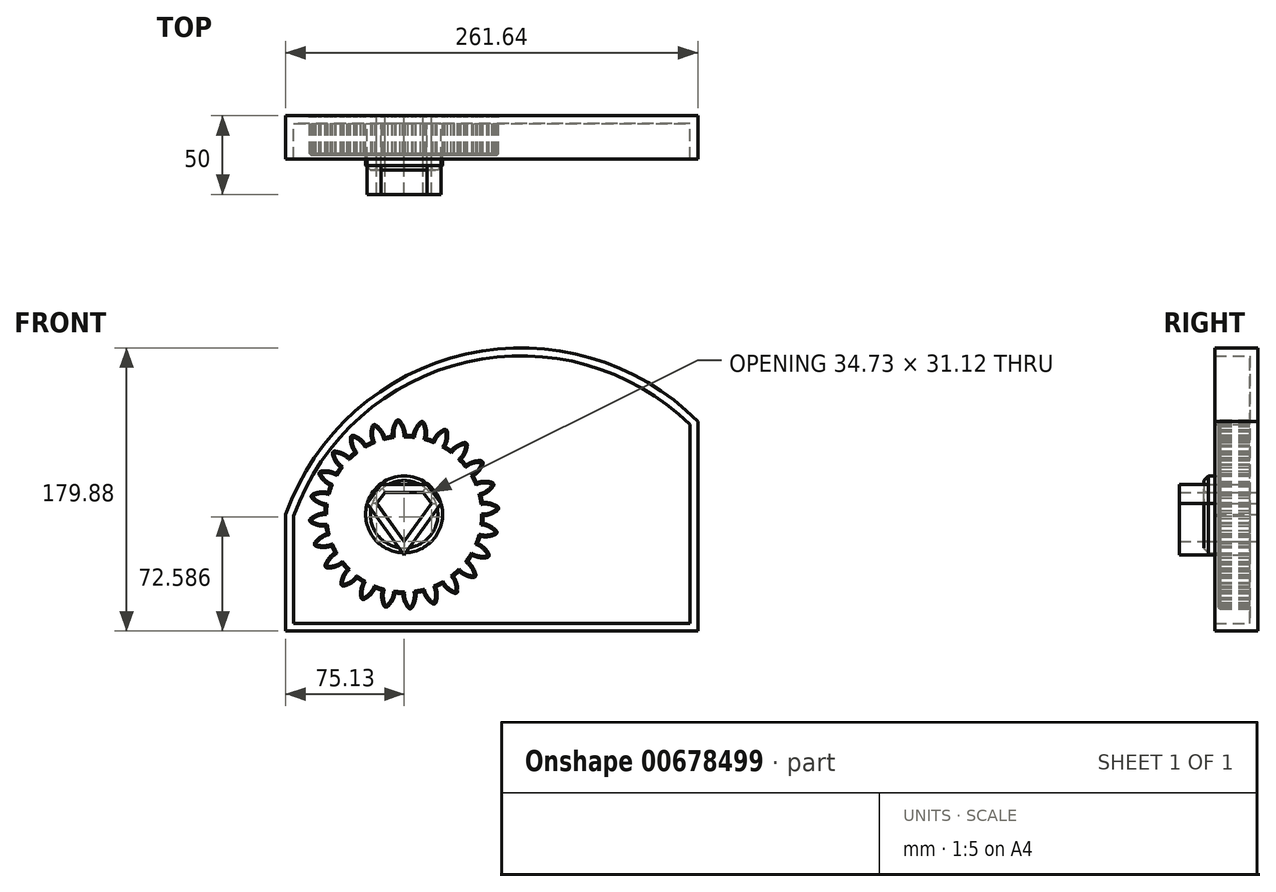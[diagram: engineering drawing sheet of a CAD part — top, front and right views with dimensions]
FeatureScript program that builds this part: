
annotation { "Feature Type Name" : "Feature", "Feature Type Description" : "" }
export const myFeature = defineFeature(function(context is Context, id is Id, definition is map)
    precondition{}
    {
        {
            var Q0;
            Q0=qCreatedBy(makeId("Front.planeOp"),FACE);
            var sketch = newSketch(context, id + "F0", { "sketchPlane" : qUnion([Q0])});
            skCircle(sketch, "E0", {"center": v(0, 0) * mm, "radius": 50.27 * mm});
            skCircle(sketch, "E1", {"center": v(0, 0) * mm, "radius": 54.9 * mm, "construction": true});
            skCircle(sketch, "E2", {"center": v(0, 0) * mm, "radius": 59.42 * mm, "construction": true});
            skLineSegment(sketch, "E3", {"start": v(0, 0) * mm, "end": v(0, 73.6) * mm, "construction": true});
            skLineSegment(sketch, "E4", {"start": v(0, 0) * mm, "end": v(-4.82, 73.6) * mm, "construction": true});
            skLineSegment(sketch, "E5", {"start": v(0, 54.9) * mm, "end": v(-59.15, 54.9) * mm, "construction": true});
            skLineSegment(sketch, "E6", {"start": v(0, 54.9) * mm, "end": v(-59.15, 33.38) * mm, "construction": true});
            skCircle(sketch, "E7", {"center": v(0, 0) * mm, "radius": 51.6 * mm, "construction": true});
            skCircle(sketch, "E8", {"center": v(0, 54.9) * mm, "radius": 14.6 * mm, "construction": true});
            skCircle(sketch, "E9", {"center": v(-13.72, 49.91) * mm, "radius": 14.6 * mm, "construction": true});
            skArc(sketch, "E10", {"start": v(0, 54.9) * mm, "mid": v(-1.1, 57.25) * mm, "end": v(-2.6, 59.37) * mm});
            skArc(sketch, "E11", {"start": v(0.88, 50.27) * mm, "mid": v(0.63, 52.62) * mm, "end": v(0, 54.9) * mm});
            skArc(sketch, "E12.MirrorCS", {"start": v(-7.17, 54.44) * mm, "mid": v(-6.38, 56.9) * mm, "end": v(-5.18, 59.2) * mm});
            skArc(sketch, "E13.MirrorCS", {"start": v(-7.43, 49.72) * mm, "mid": v(-7.5, 52.1) * mm, "end": v(-7.17, 54.44) * mm});
            skArc(sketch, "E14", {"start": v(-2.6, 59.37) * mm, "mid": v(-3.93, 59.96) * mm, "end": v(-5.18, 59.2) * mm});
            skCircle(sketch, "E15", {"center": v(0, 0) * mm, "radius": 24.42 * mm});
            skLineSegment(sketch, "E16", {"start": v(-0.11, 14.02) * mm, "end": v(-12.06, 14.02) * mm});
            skLineSegment(sketch, "E17", {"start": v(-17.36, 7.04) * mm, "end": v(-12.06, 14.02) * mm});
            skLineSegment(sketch, "E18.MirrorCS", {"start": v(17.36, 7.04) * mm, "end": v(12.06, 14.02) * mm});
            skLineSegment(sketch, "E19.MirrorCS", {"start": v(0.11, 14.02) * mm, "end": v(12.06, 14.02) * mm});
            skLineSegment(sketch, "E20", {"start": v(-0.11, -14.36) * mm, "end": v(0, -14.5) * mm});
            skLineSegment(sketch, "E21", {"start": v(0, -14.5) * mm, "end": v(0.11, -14.36) * mm});
            skLineSegment(sketch, "E22", {"start": v(-17.36, 7.04) * mm, "end": v(0, -17.1) * mm});
            skLineSegment(sketch, "E23.MirrorCS", {"start": v(17.36, 7.04) * mm, "end": v(0, -17.1) * mm});
            skLineSegment(sketch, "E24", {"start": v(-0.11, 14.02) * mm, "end": v(0.11, 14.02) * mm});
            skSolve(sketch);
        }
        {
            var Q0;
            {var subQ0=sQuery(id+"F0.wireOp",EDGE,"E0");var subQ1=makeQuery(id+"F0.imprint","INTERSECT",VERTEX,{"derivedFrom":[subQ0,sQuery(id+"F0.wireOp",EDGE,"E11")]});Q0=makeQuery(id+"F0.imprint","IMPRINT",FACE,{"disambiguationData":[TD([[makeQuery(id+"F0.imprint","IMPRINT",EDGE,{"disambiguationData":[TD([[subQ1,-1.0]])],"derivedFrom":subQ0}),1.0]])]});}
            var Q1;
            Q1=makeQuery(id+"F0.imprint","IMPRINT",FACE,{"disambiguationData":[TD([[makeQuery(id+"F0.imprint","IMPRINT",EDGE,{"derivedFrom":sQuery(id+"F0.wireOp",EDGE,"E10")}),1.0]])]});
            extrude(context, id + "F1", {"entities" : qUnion([Q0, Q1]), "depth" : 25 * mm, "offsetDistance" : 25 * mm});
        }
        {
            var Q0;
            Q0=makeQuery(id+"F1.opExtrude","CAP_EDGE",EDGE,{"disambiguationData":[OSD([sQuery(id+"F0.wireOp",EDGE,"E0")])],"isStart":false});
            var Q1;
            Q1=makeQuery(id+"F1.opExtrude","CAP_EDGE",EDGE,{"disambiguationData":[OSD([sQuery(id+"F0.wireOp",EDGE,"E11")])],"isStart":false});
            var Q2;
            Q2=makeQuery(id+"F1.opExtrude","CAP_EDGE",EDGE,{"disambiguationData":[OSD([sQuery(id+"F0.wireOp",EDGE,"E13.MirrorCS")])],"isStart":false});
            var Q3;
            Q3=makeQuery(id+"F1.opExtrude","CAP_EDGE",EDGE,{"disambiguationData":[OSD([sQuery(id+"F0.wireOp",EDGE,"E10")])],"isStart":false});
            var Q4;
            Q4=makeQuery(id+"F1.opExtrude","CAP_EDGE",EDGE,{"disambiguationData":[OSD([sQuery(id+"F0.wireOp",EDGE,"E12.MirrorCS")])],"isStart":false});
            var Q5;
            Q5=makeQuery(id+"F1.opExtrude","CAP_EDGE",EDGE,{"disambiguationData":[OSD([sQuery(id+"F0.wireOp",EDGE,"E14")])],"isStart":false});
            chamfer(context, id + "F2", {"entities" : qUnion([Q0, Q1, Q2, Q3, Q4, Q5]), "width" : 1 * mm, "tangentPropagation" : true});
        }
        {
            var Q0;
            Q0=makeQuery(id+"F1.opExtrude","SWEPT_BODY",BODY,{"disambiguationData":[OSD([sQuery(id+"F0.wireOp",EDGE,"E0"),sQuery(id+"F0.wireOp",EDGE,"E10"),sQuery(id+"F0.wireOp",EDGE,"E11"),sQuery(id+"F0.wireOp",EDGE,"E12.MirrorCS"),sQuery(id+"F0.wireOp",EDGE,"E13.MirrorCS"),sQuery(id+"F0.wireOp",EDGE,"E14"),sQuery(id+"F0.wireOp",EDGE,"E15")])]});
            var Q1;
            Q1=makeQuery(id+"F1.opExtrude","SWEPT_FACE",FACE,{"disambiguationData":[OSD([sQuery(id+"F0.wireOp",EDGE,"E0")])]});
            circularPattern(context, id + "F3", {"entities" : qUnion([Q0]), "axis" : qUnion([Q1]), "angle" : 360 * degree, "instanceCount" : 24, "equalSpace" : true});
        }
        {
            var Q0;
            Q0=makeQuery(id+"F0.imprint","IMPRINT",FACE,{"disambiguationData":[TD([[makeQuery(id+"F0.imprint","IMPRINT",EDGE,{"derivedFrom":sQuery(id+"F0.wireOp",EDGE,"E15")}),1.0]])]});
            extrude(context, id + "F4", {"entities" : qUnion([Q0]), "operationType" : NewBodyOperationType.ADD, "depth" : 34.5 * mm, "offsetDistance" : 25 * mm});
        }
        {
            var Q0;
            Q0=makeQuery(id+"F4.opExtrude","CAP_EDGE",EDGE,{"disambiguationData":[OSD([sQuery(id+"F0.wireOp",EDGE,"E15")])],"isStart":false});
            chamfer(context, id + "F5", {"entities" : qUnion([Q0]), "width" : 3 * mm, "tangentPropagation" : true});
        }
        {
            var Q0;
            Q0=makeQuery(id+"F4.opExtrude","CAP_EDGE",EDGE,{"disambiguationData":[OSD([sQuery(id+"F0.wireOp",EDGE,"E17")])],"isStart":false});
            var Q1;
            Q1=makeQuery(id+"F4.opExtrude","CAP_EDGE",EDGE,{"disambiguationData":[OSD([sQuery(id+"F0.wireOp",EDGE,"E16"),sQuery(id+"F0.wireOp",EDGE,"E19.MirrorCS"),sQuery(id+"F0.wireOp",EDGE,"E24")])],"isStart":false});
            var Q2;
            Q2=makeQuery(id+"F4.opExtrude","CAP_EDGE",EDGE,{"disambiguationData":[OSD([sQuery(id+"F0.wireOp",EDGE,"E18.MirrorCS")])],"isStart":false});
            var Q3;
            Q3=makeQuery(id+"F4.opExtrude","CAP_EDGE",EDGE,{"disambiguationData":[OSD([sQuery(id+"F0.wireOp",EDGE,"E23.MirrorCS")])],"isStart":false});
            var Q4;
            Q4=makeQuery(id+"F4.opExtrude","CAP_EDGE",EDGE,{"disambiguationData":[OSD([sQuery(id+"F0.wireOp",EDGE,"E22")])],"isStart":false});
            fillet(context, id + "F6", {"entities" : qUnion([Q0, Q1, Q2, Q3, Q4]), "radius" : 2 * mm, "tangentPropagation" : true, "allowEdgeOverflow" : false});
        }
        {
            var Q0;
            Q0=qCreatedBy(makeId("Front.planeOp"),FACE);
            var sketch = newSketch(context, id + "F7", { "sketchPlane" : qUnion([Q0])});
            skLineSegment(sketch, "E25", {"start": v(-75.13, 0) * mm, "end": v(-75.13, -74.2) * mm});
            skLineSegment(sketch, "E26", {"start": v(-75.13, -74.2) * mm, "end": v(186.5, -74.2) * mm});
            skLineSegment(sketch, "E27", {"start": v(186.5, -74.2) * mm, "end": v(186.5, 59.11) * mm});
            skArc(sketch, "E28", {"start": v(186.5, 59.11) * mm, "mid": v(39.37, 101.8) * mm, "end": v(-75.13, 0) * mm});
            skLineSegment(sketch, "E29", {"start": v(-0.11, 13.95) * mm, "end": v(-12.06, 13.95) * mm});
            skLineSegment(sketch, "E30", {"start": v(-17.36, 6.98) * mm, "end": v(-12.06, 13.95) * mm});
            skLineSegment(sketch, "E31.MirrorCS", {"start": v(17.36, 6.98) * mm, "end": v(12.06, 13.95) * mm});
            skLineSegment(sketch, "E32.MirrorCS", {"start": v(0.11, 13.95) * mm, "end": v(12.06, 13.95) * mm});
            skLineSegment(sketch, "E33", {"start": v(-17.36, 6.98) * mm, "end": v(0, -17.16) * mm});
            skLineSegment(sketch, "E34.MirrorCS", {"start": v(17.36, 6.98) * mm, "end": v(0, -17.16) * mm});
            skLineSegment(sketch, "E35", {"start": v(-0.11, 13.95) * mm, "end": v(0.11, 13.95) * mm});
            skSolve(sketch);
        }
        {
            var Q0;
            Q0 = qSketchRegion(id + "F7", true);
            extrude(context, id + "F8", {"entities" : qUnion([Q0]), "depth" : 50 * mm, "offsetDistance" : 25 * mm});
        }
        {
            var Q0;
            Q0=makeQuery(id+"F8.opExtrude","CAP_FACE",FACE,{"disambiguationData":[OSD([sQuery(id+"F7.wireOp",EDGE,"E25"),sQuery(id+"F7.wireOp",EDGE,"E26"),sQuery(id+"F7.wireOp",EDGE,"E27"),sQuery(id+"F7.wireOp",EDGE,"E28"),sQuery(id+"F7.wireOp",EDGE,"fd4b1a9f-0bb5-4822-8504-ba3fec9640b8"),sQuery(id+"F7.wireOp",EDGE,"4ddbff50-2f28-4b71-a308-cb6bcf8660a9"),sQuery(id+"F7.wireOp",EDGE,"22ddce49-a7ba-4eb5-bec9-ac5769881b4c.MirrorCS"),sQuery(id+"F7.wireOp",EDGE,"944a07d1-e20c-4ca9-ae79-bcf0847265d0.MirrorCS"),sQuery(id+"F7.wireOp",EDGE,"78f842e8-e3ab-41d6-b96a-d42fc7fecef2"),sQuery(id+"F7.wireOp",EDGE,"4ec05e8d-18c9-4f36-bc6d-69da79d936e7.MirrorCS"),sQuery(id+"F7.wireOp",EDGE,"b885e508-7b36-463d-9561-ba7b01d0f901")])],"isStart":false});
            shell(context, id + "F9", {"entities" : qUnion([Q0]), "thickness" : 5 * mm});
        }
        {
            var Q0;
            Q0=makeQuery(id+"F8.opExtrude","CAP_FACE",FACE,{"disambiguationData":[OSD([sQuery(id+"F7.wireOp",EDGE,"E25"),sQuery(id+"F7.wireOp",EDGE,"E26"),sQuery(id+"F7.wireOp",EDGE,"E27"),sQuery(id+"F7.wireOp",EDGE,"E28"),sQuery(id+"F7.wireOp",EDGE,"E29"),sQuery(id+"F7.wireOp",EDGE,"E30"),sQuery(id+"F7.wireOp",EDGE,"E31.MirrorCS"),sQuery(id+"F7.wireOp",EDGE,"E32.MirrorCS"),sQuery(id+"F7.wireOp",EDGE,"E33"),sQuery(id+"F7.wireOp",EDGE,"E34.MirrorCS"),sQuery(id+"F7.wireOp",EDGE,"E35")])],"isStart":false});
            extrude(context, id + "F10", {"entities" : qUnion([Q0]), "operationType" : NewBodyOperationType.REMOVE, "oppositeDirection" : true, "depth" : 22.5 * mm, "offsetDistance" : 25 * mm});
        }
    });
